# Revit family: STANDARD RGB 5050 IP68_LHRGBEXT
name_source: partatom
category: Luminarias
units: mm (PartAtom-declared; Revit-internal decimal feet)

## family parameters
Compartido = No
Corte con vacíos al cargar = No
Cota de conector redondo = Diámetro de uso
Origen de luz = Sí
Punto de cálculo de habitación = No
Se basa en plano de trabajo = Sí
Siempre vertical = No
Tipo de pieza = Normal

## types (1)
- STANDARD RGB 5050 IP68_LHRGBEXT
    Cambio de temperatura de color de luz atenuada = <Ninguno>
    Comentarios de vataje = 12
    Descripción = TIRA LUMINOSA STANDARD RGB 5050 DE UN MATERIAL PCB COBRE CON RECUBRIMIENTO DE PLASTICO, CON UNA POTENCIA DE 12W/M DE UN TIPO DE LED 5050 SMD, USO PARA EXTERIORES IP68, IRC80, 60 LEDS POR METRO, PRESENTACION DE 5M, CORTE 5CM, DISPONIBLE  PARA ATENUACION, ALIMENTADO A 12V, REQUIERE ACCESORIOS.
    Elevación por defecto = 0 mm  [stored 0 ft]
    Fabricante = BRILLANT
    Filtro de color = 16777215
    Longitud de línea de emisión = 600 mm
    Marca = BRILLANT
    Modelo = LHRGBEXT
    Modelo Lampara = 5050 SMD
    Tamaño de símbolo de origen de luz = 610 mm

note: [stored X ft] marks values corroborated as IEEE doubles in the binary element streams (Revit-internal decimal feet)

## geometry (parser evidence)
native form markers: Blend x2
no freeform markers — native parametric forms only
